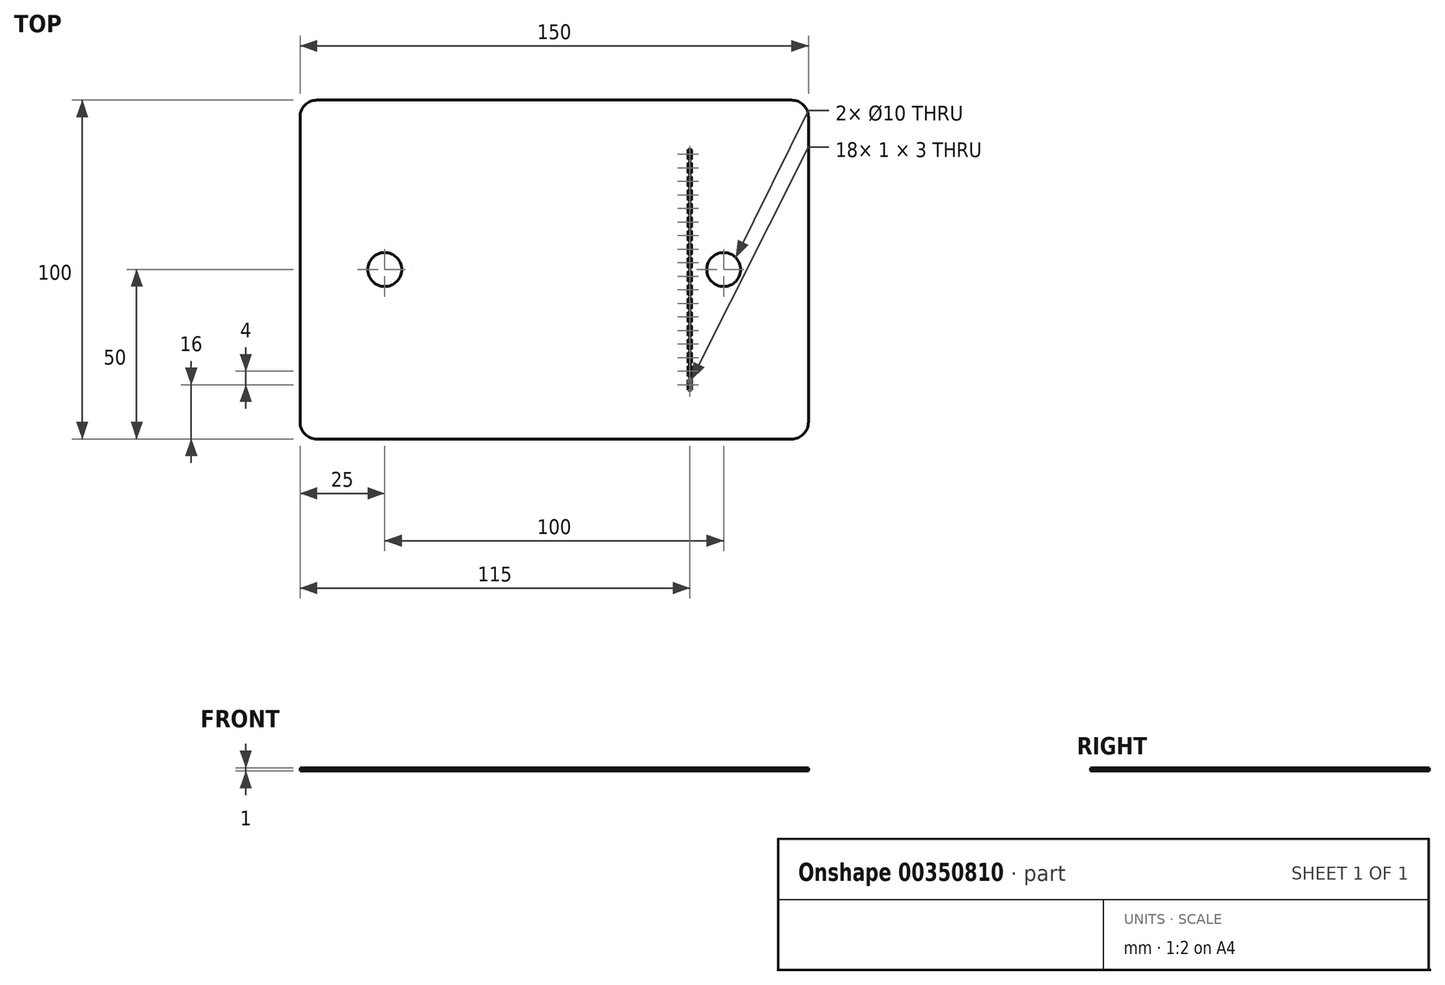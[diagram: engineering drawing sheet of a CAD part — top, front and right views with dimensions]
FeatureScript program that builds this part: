
annotation { "Feature Type Name" : "Feature", "Feature Type Description" : "" }
export const myFeature = defineFeature(function(context is Context, id is Id, definition is map)
    precondition{}
    {
        {
            var Q0;
            Q0=qCreatedBy(makeId("Top.planeOp"),FACE);
            var sketch = newSketch(context, id + "F0", { "sketchPlane" : qUnion([Q0])});
            skLineSegment(sketch, "E0.bottom", {"start": v(70, 50) * mm, "end": v(-70, 50) * mm});
            skLineSegment(sketch, "E0.top", {"start": v(70, -50) * mm, "end": v(-70, -50) * mm});
            skLineSegment(sketch, "E0.left", {"start": v(75, 45) * mm, "end": v(75, -45) * mm});
            skLineSegment(sketch, "E0.right", {"start": v(-75, 45) * mm, "end": v(-75, -45) * mm});
            skPoint(sketch, "E0.middle", {"position": v(0, 0) * mm});
            skPoint(sketch, "E1.visualSharp", {"position": v(-75, 50) * mm});
            skArc(sketch, "E1.filletArc", {"start": v(-70, 50) * mm, "mid": v(-73.54, 48.54) * mm, "end": v(-75, 45) * mm});
            skPoint(sketch, "E2.visualSharp", {"position": v(75, 50) * mm});
            skArc(sketch, "E2.filletArc", {"start": v(75, 45) * mm, "mid": v(73.54, 48.54) * mm, "end": v(70, 50) * mm});
            skPoint(sketch, "E3.visualSharp", {"position": v(-75, -50) * mm});
            skArc(sketch, "E3.filletArc", {"start": v(-75, -45) * mm, "mid": v(-73.54, -48.54) * mm, "end": v(-70, -50) * mm});
            skPoint(sketch, "E4.visualSharp", {"position": v(75, -50) * mm});
            skArc(sketch, "E4.filletArc", {"start": v(70, -50) * mm, "mid": v(73.54, -48.54) * mm, "end": v(75, -45) * mm});
            skCircle(sketch, "E5", {"center": v(-50, 0) * mm, "radius": 5 * mm});
            skCircle(sketch, "E6", {"center": v(50, 0) * mm, "radius": 5 * mm});
            skSolve(sketch);
        }
        {
            var Q0;
            Q0 = qSketchRegion(id + "F0", true);
            extrude(context, id + "F1", {"entities" : qUnion([Q0]), "depth" : 1 * mm});
        }
        {
            var Q0;
            Q0=makeQuery(id+"F1.opExtrude","CAP_FACE",FACE,{"disambiguationData":[OSD([sQuery(id+"F0.wireOp",EDGE,"E0.bottom"),sQuery(id+"F0.wireOp",EDGE,"E0.top"),sQuery(id+"F0.wireOp",EDGE,"E0.left"),sQuery(id+"F0.wireOp",EDGE,"E0.right"),sQuery(id+"F0.wireOp",EDGE,"E1.filletArc"),sQuery(id+"F0.wireOp",EDGE,"E2.filletArc"),sQuery(id+"F0.wireOp",EDGE,"E3.filletArc"),sQuery(id+"F0.wireOp",EDGE,"E4.filletArc"),sQuery(id+"F0.wireOp",EDGE,"E5"),sQuery(id+"F0.wireOp",EDGE,"E6")])],"isStart":false});
            var sketch = newSketch(context, id + "F2", { "sketchPlane" : qUnion([Q0])});
            skLineSegment(sketch, "E7.bottom", {"start": v(-75, 5) * mm, "end": v(-76, 5) * mm});
            skLineSegment(sketch, "E7.top", {"start": v(-75, -5) * mm, "end": v(-76, -5) * mm});
            skLineSegment(sketch, "E7.left", {"start": v(-75, 5) * mm, "end": v(-75, -5) * mm});
            skLineSegment(sketch, "E7.right", {"start": v(-76, 5) * mm, "end": v(-76, -5) * mm});
            skLineSegment(sketch, "E8.bottom", {"start": v(75, 5) * mm, "end": v(76, 5) * mm});
            skLineSegment(sketch, "E8.top", {"start": v(75, -5) * mm, "end": v(76, -5) * mm});
            skLineSegment(sketch, "E8.left", {"start": v(75, 5) * mm, "end": v(75, -5) * mm});
            skLineSegment(sketch, "E8.right", {"start": v(76, 5) * mm, "end": v(76, -5) * mm});
            skLineSegment(sketch, "E9.bottom", {"start": v(-5, 50) * mm, "end": v(5, 50) * mm});
            skLineSegment(sketch, "E9.top", {"start": v(-5, 51) * mm, "end": v(5, 51) * mm});
            skLineSegment(sketch, "E9.left", {"start": v(-5, 50) * mm, "end": v(-5, 51) * mm});
            skLineSegment(sketch, "E9.right", {"start": v(5, 50) * mm, "end": v(5, 51) * mm});
            skLineSegment(sketch, "E10.bottom", {"start": v(-5, -50) * mm, "end": v(5, -50) * mm});
            skLineSegment(sketch, "E10.top", {"start": v(-5, -51) * mm, "end": v(5, -51) * mm});
            skLineSegment(sketch, "E10.left", {"start": v(-5, -50) * mm, "end": v(-5, -51) * mm});
            skLineSegment(sketch, "E10.right", {"start": v(5, -50) * mm, "end": v(5, -51) * mm});
            skSolve(sketch);
        }
        {
            var Q0;
            Q0=makeQuery(id+"F0YfDiYtAgtzgQZ_1.boolean.opBoolean","MERGE",FACE,{"derivedFrom":[makeQuery(id+"F1.opExtrude","CAP_FACE",FACE,{"disambiguationData":[OSD([sQuery(id+"F0.wireOp",EDGE,"E0.bottom"),sQuery(id+"F0.wireOp",EDGE,"E0.top"),sQuery(id+"F0.wireOp",EDGE,"E0.left"),sQuery(id+"F0.wireOp",EDGE,"E0.right"),sQuery(id+"F0.wireOp",EDGE,"E1.filletArc"),sQuery(id+"F0.wireOp",EDGE,"E2.filletArc"),sQuery(id+"F0.wireOp",EDGE,"E3.filletArc"),sQuery(id+"F0.wireOp",EDGE,"E4.filletArc"),sQuery(id+"F0.wireOp",EDGE,"E5"),sQuery(id+"F0.wireOp",EDGE,"E6")])],"isStart":false}),makeQuery(id+"F0YfDiYtAgtzgQZ_1.opExtrude","CAP_FACE",FACE,{"disambiguationData":[OSD([sQuery(id+"F2.wireOp",EDGE,"E7.bottom"),sQuery(id+"F2.wireOp",EDGE,"E7.top"),sQuery(id+"F2.wireOp",EDGE,"E7.left"),sQuery(id+"F2.wireOp",EDGE,"E7.right")])],"isStart":true}),makeQuery(id+"F0YfDiYtAgtzgQZ_1.opExtrude","CAP_FACE",FACE,{"disambiguationData":[OSD([sQuery(id+"F2.wireOp",EDGE,"E8.bottom"),sQuery(id+"F2.wireOp",EDGE,"E8.top"),sQuery(id+"F2.wireOp",EDGE,"E8.left"),sQuery(id+"F2.wireOp",EDGE,"E8.right")])],"isStart":true}),makeQuery(id+"F0YfDiYtAgtzgQZ_1.opExtrude","CAP_FACE",FACE,{"disambiguationData":[OSD([sQuery(id+"F2.wireOp",EDGE,"E9.bottom"),sQuery(id+"F2.wireOp",EDGE,"E9.top"),sQuery(id+"F2.wireOp",EDGE,"E9.left"),sQuery(id+"F2.wireOp",EDGE,"E9.right")])],"isStart":true}),makeQuery(id+"F0YfDiYtAgtzgQZ_1.opExtrude","CAP_FACE",FACE,{"disambiguationData":[OSD([sQuery(id+"F2.wireOp",EDGE,"E10.bottom"),sQuery(id+"F2.wireOp",EDGE,"E10.top"),sQuery(id+"F2.wireOp",EDGE,"E10.left"),sQuery(id+"F2.wireOp",EDGE,"E10.right")])],"isStart":true})]});
            var sketch = newSketch(context, id + "F3", { "sketchPlane" : qUnion([Q0])});
            skLineSegment(sketch, "E11.bottom", {"start": v(39.5, 35.5) * mm, "end": v(40.5, 35.5) * mm});
            skLineSegment(sketch, "E11.top", {"start": v(39.5, 32.5) * mm, "end": v(40.5, 32.5) * mm});
            skLineSegment(sketch, "E11.left", {"start": v(39.5, 35.5) * mm, "end": v(39.5, 32.5) * mm});
            skLineSegment(sketch, "E11.right", {"start": v(40.5, 35.5) * mm, "end": v(40.5, 32.5) * mm});
            skLineSegment(sketch, "E12.1.0.0", {"start": v(40.5, 31.5) * mm, "end": v(40.5, 28.5) * mm});
            skLineSegment(sketch, "E12.1.0.1", {"start": v(39.5, 31.5) * mm, "end": v(40.5, 31.5) * mm});
            skLineSegment(sketch, "E12.1.0.2", {"start": v(39.5, 31.5) * mm, "end": v(39.5, 28.5) * mm});
            skLineSegment(sketch, "E12.1.0.3", {"start": v(39.5, 28.5) * mm, "end": v(40.5, 28.5) * mm});
            skLineSegment(sketch, "E12.2.0.0", {"start": v(40.5, 27.5) * mm, "end": v(40.5, 24.5) * mm});
            skLineSegment(sketch, "E12.2.0.1", {"start": v(39.5, 27.5) * mm, "end": v(40.5, 27.5) * mm});
            skLineSegment(sketch, "E12.2.0.2", {"start": v(39.5, 27.5) * mm, "end": v(39.5, 24.5) * mm});
            skLineSegment(sketch, "E12.2.0.3", {"start": v(39.5, 24.5) * mm, "end": v(40.5, 24.5) * mm});
            skLineSegment(sketch, "E12.3.0.0", {"start": v(40.5, 23.5) * mm, "end": v(40.5, 20.5) * mm});
            skLineSegment(sketch, "E12.3.0.1", {"start": v(39.5, 23.5) * mm, "end": v(40.5, 23.5) * mm});
            skLineSegment(sketch, "E12.3.0.2", {"start": v(39.5, 23.5) * mm, "end": v(39.5, 20.5) * mm});
            skLineSegment(sketch, "E12.3.0.3", {"start": v(39.5, 20.5) * mm, "end": v(40.5, 20.5) * mm});
            skLineSegment(sketch, "E12.4.0.0", {"start": v(40.5, 19.5) * mm, "end": v(40.5, 16.5) * mm});
            skLineSegment(sketch, "E12.4.0.1", {"start": v(39.5, 19.5) * mm, "end": v(40.5, 19.5) * mm});
            skLineSegment(sketch, "E12.4.0.2", {"start": v(39.5, 19.5) * mm, "end": v(39.5, 16.5) * mm});
            skLineSegment(sketch, "E12.4.0.3", {"start": v(39.5, 16.5) * mm, "end": v(40.5, 16.5) * mm});
            skLineSegment(sketch, "E12.5.0.0", {"start": v(40.5, 15.5) * mm, "end": v(40.5, 12.5) * mm});
            skLineSegment(sketch, "E12.5.0.1", {"start": v(39.5, 15.5) * mm, "end": v(40.5, 15.5) * mm});
            skLineSegment(sketch, "E12.5.0.2", {"start": v(39.5, 15.5) * mm, "end": v(39.5, 12.5) * mm});
            skLineSegment(sketch, "E12.5.0.3", {"start": v(39.5, 12.5) * mm, "end": v(40.5, 12.5) * mm});
            skLineSegment(sketch, "E12.6.0.0", {"start": v(40.5, 11.5) * mm, "end": v(40.5, 8.5) * mm});
            skLineSegment(sketch, "E12.6.0.1", {"start": v(39.5, 11.5) * mm, "end": v(40.5, 11.5) * mm});
            skLineSegment(sketch, "E12.6.0.2", {"start": v(39.5, 11.5) * mm, "end": v(39.5, 8.5) * mm});
            skLineSegment(sketch, "E12.6.0.3", {"start": v(39.5, 8.5) * mm, "end": v(40.5, 8.5) * mm});
            skLineSegment(sketch, "E12.7.0.0", {"start": v(40.5, 7.5) * mm, "end": v(40.5, 4.5) * mm});
            skLineSegment(sketch, "E12.7.0.1", {"start": v(39.5, 7.5) * mm, "end": v(40.5, 7.5) * mm});
            skLineSegment(sketch, "E12.7.0.2", {"start": v(39.5, 7.5) * mm, "end": v(39.5, 4.5) * mm});
            skLineSegment(sketch, "E12.7.0.3", {"start": v(39.5, 4.5) * mm, "end": v(40.5, 4.5) * mm});
            skLineSegment(sketch, "E12.8.0.0", {"start": v(40.5, 3.5) * mm, "end": v(40.5, 0.5) * mm});
            skLineSegment(sketch, "E12.8.0.1", {"start": v(39.5, 3.5) * mm, "end": v(40.5, 3.5) * mm});
            skLineSegment(sketch, "E12.8.0.2", {"start": v(39.5, 3.5) * mm, "end": v(39.5, 0.5) * mm});
            skLineSegment(sketch, "E12.8.0.3", {"start": v(39.5, 0.5) * mm, "end": v(40.5, 0.5) * mm});
            skLineSegment(sketch, "E12.9.0.0", {"start": v(40.5, -0.5) * mm, "end": v(40.5, -3.5) * mm});
            skLineSegment(sketch, "E12.9.0.1", {"start": v(39.5, -0.5) * mm, "end": v(40.5, -0.5) * mm});
            skLineSegment(sketch, "E12.9.0.2", {"start": v(39.5, -0.5) * mm, "end": v(39.5, -3.5) * mm});
            skLineSegment(sketch, "E12.9.0.3", {"start": v(39.5, -3.5) * mm, "end": v(40.5, -3.5) * mm});
            skLineSegment(sketch, "E12.10.0.0", {"start": v(40.5, -4.5) * mm, "end": v(40.5, -7.5) * mm});
            skLineSegment(sketch, "E12.10.0.1", {"start": v(39.5, -4.5) * mm, "end": v(40.5, -4.5) * mm});
            skLineSegment(sketch, "E12.10.0.2", {"start": v(39.5, -4.5) * mm, "end": v(39.5, -7.5) * mm});
            skLineSegment(sketch, "E12.10.0.3", {"start": v(39.5, -7.5) * mm, "end": v(40.5, -7.5) * mm});
            skLineSegment(sketch, "E12.11.0.0", {"start": v(40.5, -8.5) * mm, "end": v(40.5, -11.5) * mm});
            skLineSegment(sketch, "E12.11.0.1", {"start": v(39.5, -8.5) * mm, "end": v(40.5, -8.5) * mm});
            skLineSegment(sketch, "E12.11.0.2", {"start": v(39.5, -8.5) * mm, "end": v(39.5, -11.5) * mm});
            skLineSegment(sketch, "E12.11.0.3", {"start": v(39.5, -11.5) * mm, "end": v(40.5, -11.5) * mm});
            skLineSegment(sketch, "E12.12.0.0", {"start": v(40.5, -12.5) * mm, "end": v(40.5, -15.5) * mm});
            skLineSegment(sketch, "E12.12.0.1", {"start": v(39.5, -12.5) * mm, "end": v(40.5, -12.5) * mm});
            skLineSegment(sketch, "E12.12.0.2", {"start": v(39.5, -12.5) * mm, "end": v(39.5, -15.5) * mm});
            skLineSegment(sketch, "E12.12.0.3", {"start": v(39.5, -15.5) * mm, "end": v(40.5, -15.5) * mm});
            skLineSegment(sketch, "E12.13.0.0", {"start": v(40.5, -16.5) * mm, "end": v(40.5, -19.5) * mm});
            skLineSegment(sketch, "E12.13.0.1", {"start": v(39.5, -16.5) * mm, "end": v(40.5, -16.5) * mm});
            skLineSegment(sketch, "E12.13.0.2", {"start": v(39.5, -16.5) * mm, "end": v(39.5, -19.5) * mm});
            skLineSegment(sketch, "E12.13.0.3", {"start": v(39.5, -19.5) * mm, "end": v(40.5, -19.5) * mm});
            skLineSegment(sketch, "E12.14.0.0", {"start": v(40.5, -20.5) * mm, "end": v(40.5, -23.5) * mm});
            skLineSegment(sketch, "E12.14.0.1", {"start": v(39.5, -20.5) * mm, "end": v(40.5, -20.5) * mm});
            skLineSegment(sketch, "E12.14.0.2", {"start": v(39.5, -20.5) * mm, "end": v(39.5, -23.5) * mm});
            skLineSegment(sketch, "E12.14.0.3", {"start": v(39.5, -23.5) * mm, "end": v(40.5, -23.5) * mm});
            skLineSegment(sketch, "E12.15.0.0", {"start": v(40.5, -24.5) * mm, "end": v(40.5, -27.5) * mm});
            skLineSegment(sketch, "E12.15.0.1", {"start": v(39.5, -24.5) * mm, "end": v(40.5, -24.5) * mm});
            skLineSegment(sketch, "E12.15.0.2", {"start": v(39.5, -24.5) * mm, "end": v(39.5, -27.5) * mm});
            skLineSegment(sketch, "E12.15.0.3", {"start": v(39.5, -27.5) * mm, "end": v(40.5, -27.5) * mm});
            skLineSegment(sketch, "E12.16.0.0", {"start": v(40.5, -28.5) * mm, "end": v(40.5, -31.5) * mm});
            skLineSegment(sketch, "E12.16.0.1", {"start": v(39.5, -28.5) * mm, "end": v(40.5, -28.5) * mm});
            skLineSegment(sketch, "E12.16.0.2", {"start": v(39.5, -28.5) * mm, "end": v(39.5, -31.5) * mm});
            skLineSegment(sketch, "E12.16.0.3", {"start": v(39.5, -31.5) * mm, "end": v(40.5, -31.5) * mm});
            skLineSegment(sketch, "E12.17.0.0", {"start": v(40.5, -32.5) * mm, "end": v(40.5, -35.5) * mm});
            skLineSegment(sketch, "E12.17.0.1", {"start": v(39.5, -32.5) * mm, "end": v(40.5, -32.5) * mm});
            skLineSegment(sketch, "E12.17.0.2", {"start": v(39.5, -32.5) * mm, "end": v(39.5, -35.5) * mm});
            skLineSegment(sketch, "E12.17.0.3", {"start": v(39.5, -35.5) * mm, "end": v(40.5, -35.5) * mm});
            skLineSegment(sketch, "E12.direction1", {"start": v(40.5, 32.5) * mm, "end": v(40.5, 28.5) * mm, "construction": true});
            skLineSegment(sketch, "E13", {"start": v(40, 35.5) * mm, "end": v(40, -35.5) * mm, "construction": true});
            skSolve(sketch);
        }
        {
            var Q0;
            Q0 = qSketchRegion(id + "F3", true);
            extrude(context, id + "F4", {"entities" : qUnion([Q0]), "operationType" : NewBodyOperationType.REMOVE, "endBound" : BoundingType.THROUGH_ALL, "oppositeDirection" : true, "depth" : 25 * mm});
        }
    });
